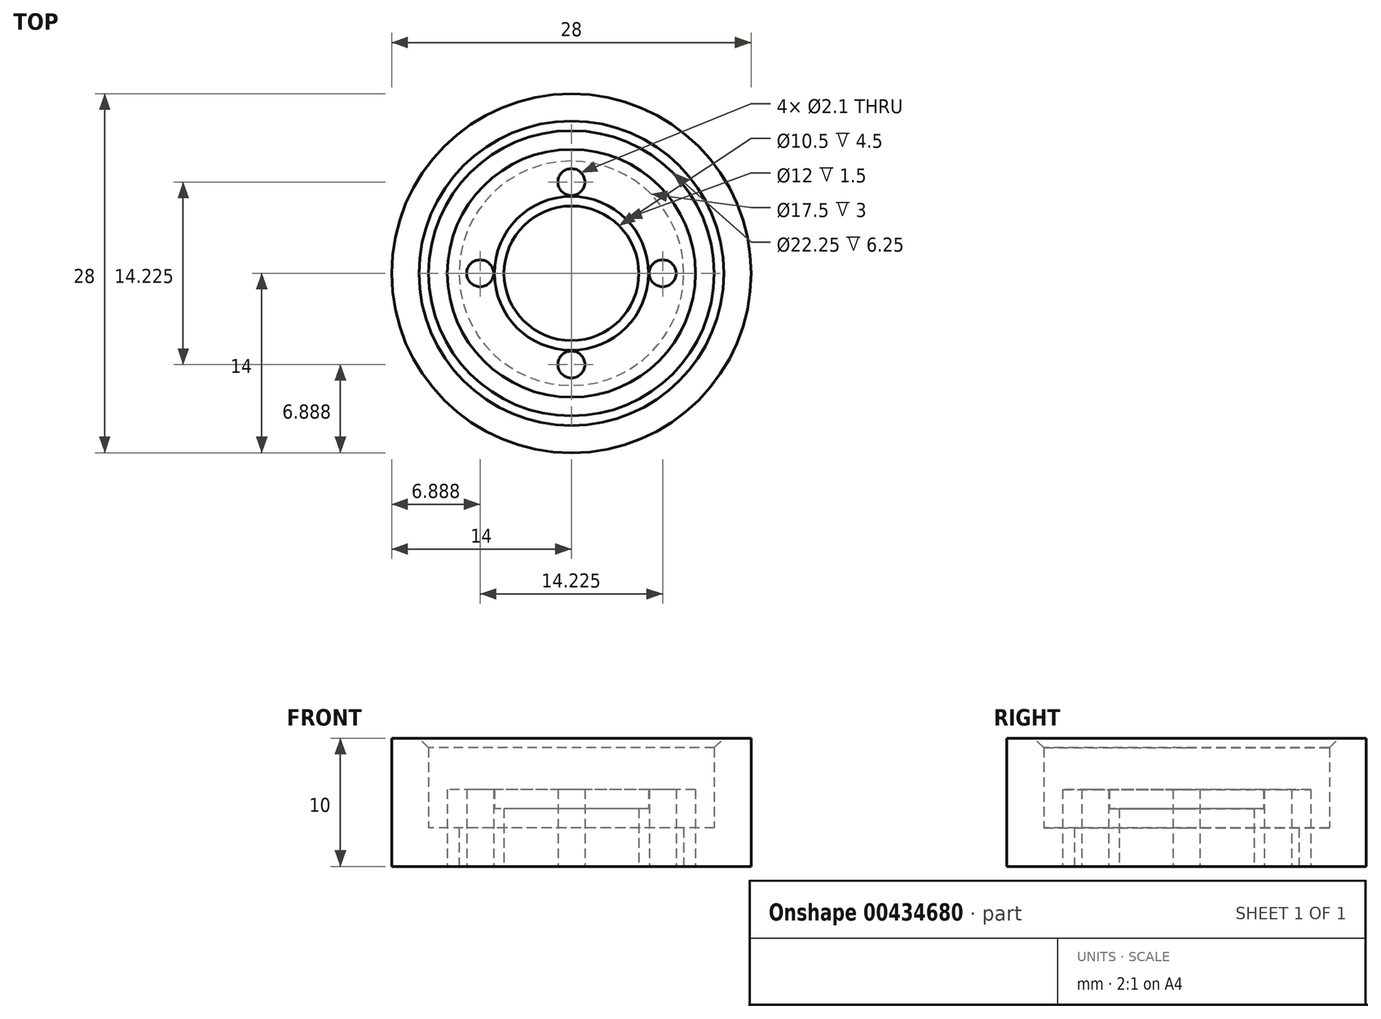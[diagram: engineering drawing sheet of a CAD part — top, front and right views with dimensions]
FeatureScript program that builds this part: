
annotation { "Feature Type Name" : "Feature", "Feature Type Description" : "" }
export const myFeature = defineFeature(function(context is Context, id is Id, definition is map)
    precondition{}
    {
        {
            assignVariable(context, id + "F0", {"name" : "BearingThickness", "anyValue" : 4});
        }
        {
            assignVariable(context, id + "F1", {"name" : "BearingDiameter", "anyValue" : 10.5});
        }
        {
            assignVariable(context, id + "F2", {"name" : "FlangeDiameter", "anyValue" : 12});
        }
        {
            assignVariable(context, id + "F3", {"name" : "FlangeThickness", "anyValue" : getVariable(context, 'FlangeDiameter') - getVariable(context, 'BearingDiameter')});
        }
        {
            assignVariable(context, id + "F4", {"name" : "HoleDiameter", "anyValue" : 2.1});
        }
        {
            assignVariable(context, id + "F5", {"name" : "HubThickness", "anyValue" : 0.5 + getVariable(context, 'BearingThickness') + getVariable(context, 'FlangeThickness')});
        }
        {
            var Q0;
            Q0=qCreatedBy(makeId("Top.planeOp"),FACE);
            var sketch = newSketch(context, id + "F6", { "sketchPlane" : qUnion([Q0])});
            skLineSegment(sketch, "E0", {"start": v(-35.9, 0) * mm, "end": v(35.9, 0) * mm, "construction": true});
            skLineSegment(sketch, "E1", {"start": v(0, 35.9) * mm, "end": v(0, -35.9) * mm, "construction": true});
            skCircle(sketch, "E2", {"center": v(0, 0) * mm, "radius": 5.25 * mm});
            skCircle(sketch, "E3", {"center": v(0, 0) * mm, "radius": 6 * mm});
            skCircle(sketch, "E4", {"center": v(0, 0) * mm, "radius": 6.06 * mm, "construction": true});
            skCircle(sketch, "E5.0", {"center": v(0, 0) * mm, "radius": 35.9 * mm});
            skCircle(sketch, "E6", {"center": v(-7.11, 0) * mm, "radius": 1.05 * mm, "construction": true});
            skCircle(sketch, "E7", {"center": v(0, 7.11) * mm, "radius": 1.05 * mm, "construction": true});
            skCircle(sketch, "E8.MirrorC", {"center": v(7.11, 0) * mm, "radius": 1.05 * mm, "construction": true});
            skCircle(sketch, "E9.MirrorC", {"center": v(0, -7.11) * mm, "radius": 1.05 * mm, "construction": true});
            skCircle(sketch, "E10", {"center": v(0, 0) * mm, "radius": 8.16 * mm, "construction": true});
            skCircle(sketch, "E11", {"center": v(0, 0) * mm, "radius": 9.66 * mm});
            skCircle(sketch, "E12.0", {"center": v(0, 0) * mm, "radius": 32.9 * mm});
            skLineSegment(sketch, "E12.1", {"start": v(-1.5, 39.75) * mm, "end": v(-1.5, 35.87) * mm});
            skLineSegment(sketch, "E12.2", {"start": v(1.5, 39.75) * mm, "end": v(1.5, 35.87) * mm});
            skArc(sketch, "E12.3", {"start": v(-0.3, 40.91) * mm, "mid": v(-1.15, 40.59) * mm, "end": v(-1.5, 39.75) * mm});
            skArc(sketch, "E12.4", {"start": v(0.3, 40.91) * mm, "mid": v(1.15, 40.59) * mm, "end": v(1.5, 39.75) * mm});
            skLineSegment(sketch, "E12.5", {"start": v(0.3, 40.91) * mm, "end": v(0, 40.92) * mm});
            skLineSegment(sketch, "E12.6", {"start": v(-0.3, 40.91) * mm, "end": v(0, 40.92) * mm});
            skLineSegment(sketch, "E13.1.1", {"start": v(-17.54, 35.7) * mm, "end": v(-15.96, 32.16) * mm});
            skLineSegment(sketch, "E13.1.2", {"start": v(-14.8, 36.92) * mm, "end": v(-13.22, 33.38) * mm});
            skArc(sketch, "E13.1.3", {"start": v(-16.92, 37.26) * mm, "mid": v(-17.56, 36.61) * mm, "end": v(-17.54, 35.7) * mm});
            skArc(sketch, "E13.1.4", {"start": v(-16.37, 37.5) * mm, "mid": v(-15.46, 37.54) * mm, "end": v(-14.8, 36.92) * mm});
            skLineSegment(sketch, "E13.1.5", {"start": v(-16.92, 37.26) * mm, "end": v(-16.64, 37.38) * mm});
            skLineSegment(sketch, "E13.1.6", {"start": v(-16.37, 37.5) * mm, "end": v(-16.64, 37.38) * mm});
            skLineSegment(sketch, "E13.2.1", {"start": v(-30.54, 25.48) * mm, "end": v(-27.66, 22.89) * mm});
            skLineSegment(sketch, "E13.2.2", {"start": v(-28.54, 27.71) * mm, "end": v(-25.65, 25.12) * mm});
            skArc(sketch, "E13.2.3", {"start": v(-30.6, 27.15) * mm, "mid": v(-30.93, 26.3) * mm, "end": v(-30.54, 25.48) * mm});
            skArc(sketch, "E13.2.4", {"start": v(-30.2, 27.6) * mm, "mid": v(-29.4, 28) * mm, "end": v(-28.54, 27.71) * mm});
            skLineSegment(sketch, "E13.2.5", {"start": v(-30.6, 27.15) * mm, "end": v(-30.4, 27.38) * mm});
            skLineSegment(sketch, "E13.2.6", {"start": v(-30.2, 27.6) * mm, "end": v(-30.4, 27.38) * mm});
            skLineSegment(sketch, "E13.3.1", {"start": v(-38.27, 10.86) * mm, "end": v(-34.58, 9.66) * mm});
            skLineSegment(sketch, "E13.3.2", {"start": v(-37.34, 13.71) * mm, "end": v(-33.65, 12.51) * mm});
            skArc(sketch, "E13.3.3", {"start": v(-39, 12.36) * mm, "mid": v(-38.95, 11.45) * mm, "end": v(-38.27, 10.86) * mm});
            skArc(sketch, "E13.3.4", {"start": v(-38.82, 12.93) * mm, "mid": v(-38.25, 13.63) * mm, "end": v(-37.34, 13.71) * mm});
            skLineSegment(sketch, "E13.3.5", {"start": v(-39, 12.36) * mm, "end": v(-38.91, 12.64) * mm});
            skLineSegment(sketch, "E13.3.6", {"start": v(-38.82, 12.93) * mm, "end": v(-38.91, 12.64) * mm});
            skLineSegment(sketch, "E13.4.1", {"start": v(-39.38, -5.65) * mm, "end": v(-35.52, -5.24) * mm});
            skLineSegment(sketch, "E13.4.2", {"start": v(-39.69, -2.66) * mm, "end": v(-35.83, -2.26) * mm});
            skArc(sketch, "E13.4.3", {"start": v(-40.66, -4.58) * mm, "mid": v(-40.24, -5.38) * mm, "end": v(-39.38, -5.65) * mm});
            skArc(sketch, "E13.4.4", {"start": v(-40.72, -3.98) * mm, "mid": v(-40.48, -3.1) * mm, "end": v(-39.69, -2.66) * mm});
            skLineSegment(sketch, "E13.4.5", {"start": v(-40.66, -4.58) * mm, "end": v(-40.7, -4.28) * mm});
            skLineSegment(sketch, "E13.4.6", {"start": v(-40.72, -3.98) * mm, "end": v(-40.7, -4.28) * mm});
            skLineSegment(sketch, "E13.5.1", {"start": v(-33.67, -21.17) * mm, "end": v(-30.31, -19.23) * mm});
            skLineSegment(sketch, "E13.5.2", {"start": v(-35.17, -18.58) * mm, "end": v(-31.81, -16.64) * mm});
            skArc(sketch, "E13.5.3", {"start": v(-35.28, -20.72) * mm, "mid": v(-34.58, -21.29) * mm, "end": v(-33.67, -21.17) * mm});
            skArc(sketch, "E13.5.4", {"start": v(-35.58, -20.2) * mm, "mid": v(-35.72, -19.3) * mm, "end": v(-35.17, -18.58) * mm});
            skLineSegment(sketch, "E13.5.5", {"start": v(-35.28, -20.72) * mm, "end": v(-35.44, -20.46) * mm});
            skLineSegment(sketch, "E13.5.6", {"start": v(-35.58, -20.2) * mm, "end": v(-35.44, -20.46) * mm});
            skLineSegment(sketch, "E13.6.1", {"start": v(-22.15, -33.04) * mm, "end": v(-19.87, -29.9) * mm});
            skLineSegment(sketch, "E13.6.2", {"start": v(-24.58, -31.28) * mm, "end": v(-22.3, -28.14) * mm});
            skArc(sketch, "E13.6.3", {"start": v(-23.8, -33.28) * mm, "mid": v(-22.93, -33.5) * mm, "end": v(-22.15, -33.04) * mm});
            skArc(sketch, "E13.6.4", {"start": v(-24.3, -32.92) * mm, "mid": v(-24.78, -32.16) * mm, "end": v(-24.58, -31.28) * mm});
            skLineSegment(sketch, "E13.6.5", {"start": v(-23.8, -33.28) * mm, "end": v(-24.05, -33.1) * mm});
            skLineSegment(sketch, "E13.6.6", {"start": v(-24.3, -32.92) * mm, "end": v(-24.05, -33.1) * mm});
            skLineSegment(sketch, "E13.7.1", {"start": v(-6.8, -39.2) * mm, "end": v(-6, -35.4) * mm});
            skLineSegment(sketch, "E13.7.2", {"start": v(-9.73, -38.57) * mm, "end": v(-8.92, -34.77) * mm});
            skArc(sketch, "E13.7.3", {"start": v(-8.21, -40.08) * mm, "mid": v(-7.32, -39.94) * mm, "end": v(-6.8, -39.2) * mm});
            skArc(sketch, "E13.7.4", {"start": v(-8.8, -39.96) * mm, "mid": v(-9.56, -39.46) * mm, "end": v(-9.73, -38.57) * mm});
            skLineSegment(sketch, "E13.7.5", {"start": v(-8.21, -40.08) * mm, "end": v(-8.5, -40.02) * mm});
            skLineSegment(sketch, "E13.7.6", {"start": v(-8.8, -39.96) * mm, "end": v(-8.5, -40.02) * mm});
            skLineSegment(sketch, "E13.8.1", {"start": v(9.73, -38.57) * mm, "end": v(8.92, -34.77) * mm});
            skLineSegment(sketch, "E13.8.2", {"start": v(6.8, -39.2) * mm, "end": v(6, -35.4) * mm});
            skArc(sketch, "E13.8.3", {"start": v(8.8, -39.96) * mm, "mid": v(9.56, -39.46) * mm, "end": v(9.73, -38.57) * mm});
            skArc(sketch, "E13.8.4", {"start": v(8.21, -40.08) * mm, "mid": v(7.32, -39.94) * mm, "end": v(6.8, -39.2) * mm});
            skLineSegment(sketch, "E13.8.5", {"start": v(8.8, -39.96) * mm, "end": v(8.5, -40.02) * mm});
            skLineSegment(sketch, "E13.8.6", {"start": v(8.21, -40.08) * mm, "end": v(8.5, -40.02) * mm});
            skLineSegment(sketch, "E13.9.1", {"start": v(24.58, -31.28) * mm, "end": v(22.3, -28.14) * mm});
            skLineSegment(sketch, "E13.9.2", {"start": v(22.15, -33.04) * mm, "end": v(19.87, -29.9) * mm});
            skArc(sketch, "E13.9.3", {"start": v(24.3, -32.92) * mm, "mid": v(24.78, -32.16) * mm, "end": v(24.58, -31.28) * mm});
            skArc(sketch, "E13.9.4", {"start": v(23.8, -33.28) * mm, "mid": v(22.93, -33.5) * mm, "end": v(22.15, -33.04) * mm});
            skLineSegment(sketch, "E13.9.5", {"start": v(24.3, -32.92) * mm, "end": v(24.05, -33.1) * mm});
            skLineSegment(sketch, "E13.9.6", {"start": v(23.8, -33.28) * mm, "end": v(24.05, -33.1) * mm});
            skLineSegment(sketch, "E13.10.1", {"start": v(35.17, -18.58) * mm, "end": v(31.81, -16.64) * mm});
            skLineSegment(sketch, "E13.10.2", {"start": v(33.67, -21.17) * mm, "end": v(30.31, -19.23) * mm});
            skArc(sketch, "E13.10.3", {"start": v(35.58, -20.2) * mm, "mid": v(35.72, -19.3) * mm, "end": v(35.17, -18.58) * mm});
            skArc(sketch, "E13.10.4", {"start": v(35.28, -20.72) * mm, "mid": v(34.58, -21.29) * mm, "end": v(33.67, -21.17) * mm});
            skLineSegment(sketch, "E13.10.5", {"start": v(35.58, -20.2) * mm, "end": v(35.44, -20.46) * mm});
            skLineSegment(sketch, "E13.10.6", {"start": v(35.28, -20.72) * mm, "end": v(35.44, -20.46) * mm});
            skLineSegment(sketch, "E13.11.1", {"start": v(39.69, -2.66) * mm, "end": v(35.83, -2.26) * mm});
            skLineSegment(sketch, "E13.11.2", {"start": v(39.38, -5.65) * mm, "end": v(35.52, -5.24) * mm});
            skArc(sketch, "E13.11.3", {"start": v(40.72, -3.98) * mm, "mid": v(40.48, -3.1) * mm, "end": v(39.69, -2.66) * mm});
            skArc(sketch, "E13.11.4", {"start": v(40.66, -4.58) * mm, "mid": v(40.24, -5.38) * mm, "end": v(39.38, -5.65) * mm});
            skLineSegment(sketch, "E13.11.5", {"start": v(40.72, -3.98) * mm, "end": v(40.7, -4.28) * mm});
            skLineSegment(sketch, "E13.11.6", {"start": v(40.66, -4.58) * mm, "end": v(40.7, -4.28) * mm});
            skLineSegment(sketch, "E13.12.1", {"start": v(37.34, 13.71) * mm, "end": v(33.65, 12.51) * mm});
            skLineSegment(sketch, "E13.12.2", {"start": v(38.27, 10.86) * mm, "end": v(34.58, 9.66) * mm});
            skArc(sketch, "E13.12.3", {"start": v(38.82, 12.93) * mm, "mid": v(38.25, 13.63) * mm, "end": v(37.34, 13.71) * mm});
            skArc(sketch, "E13.12.4", {"start": v(39, 12.36) * mm, "mid": v(38.95, 11.45) * mm, "end": v(38.27, 10.86) * mm});
            skLineSegment(sketch, "E13.12.5", {"start": v(38.82, 12.93) * mm, "end": v(38.91, 12.64) * mm});
            skLineSegment(sketch, "E13.12.6", {"start": v(39, 12.36) * mm, "end": v(38.91, 12.64) * mm});
            skLineSegment(sketch, "E13.13.1", {"start": v(28.54, 27.71) * mm, "end": v(25.65, 25.12) * mm});
            skLineSegment(sketch, "E13.13.2", {"start": v(30.54, 25.48) * mm, "end": v(27.66, 22.89) * mm});
            skArc(sketch, "E13.13.3", {"start": v(30.2, 27.6) * mm, "mid": v(29.4, 28) * mm, "end": v(28.54, 27.71) * mm});
            skArc(sketch, "E13.13.4", {"start": v(30.6, 27.15) * mm, "mid": v(30.93, 26.3) * mm, "end": v(30.54, 25.48) * mm});
            skLineSegment(sketch, "E13.13.5", {"start": v(30.2, 27.6) * mm, "end": v(30.4, 27.38) * mm});
            skLineSegment(sketch, "E13.13.6", {"start": v(30.6, 27.15) * mm, "end": v(30.4, 27.38) * mm});
            skLineSegment(sketch, "E13.14.1", {"start": v(14.8, 36.92) * mm, "end": v(13.22, 33.38) * mm});
            skLineSegment(sketch, "E13.14.2", {"start": v(17.54, 35.7) * mm, "end": v(15.96, 32.16) * mm});
            skArc(sketch, "E13.14.3", {"start": v(16.37, 37.5) * mm, "mid": v(15.46, 37.54) * mm, "end": v(14.8, 36.92) * mm});
            skArc(sketch, "E13.14.4", {"start": v(16.92, 37.26) * mm, "mid": v(17.56, 36.61) * mm, "end": v(17.54, 35.7) * mm});
            skLineSegment(sketch, "E13.14.5", {"start": v(16.37, 37.5) * mm, "end": v(16.64, 37.38) * mm});
            skLineSegment(sketch, "E13.14.6", {"start": v(16.92, 37.26) * mm, "end": v(16.64, 37.38) * mm});
            skSolve(sketch);
        }
        {
            var Q0;
            Q0=makeQuery(id+"F6.imprint","IMPRINT",FACE,{"disambiguationData":[TD([[makeQuery(id+"F6.imprint","IMPRINT",EDGE,{"derivedFrom":sQuery(id+"F6.wireOp",EDGE,"E2")}),-1.0]])]});
            extrude(context, id + "F7", {"entities" : qUnion([Q0]), "depth" : (getVariable(context, 'HubThickness') - getVariable(context, 'FlangeThickness')) * mm});
        }
        {
            var Q0;
            Q0=makeQuery(id+"F6.imprint","IMPRINT",FACE,{"disambiguationData":[TD([[makeQuery(id+"F6.imprint","IMPRINT",EDGE,{"derivedFrom":sQuery(id+"F6.wireOp",EDGE,"E3")}),-1.0]])]});
            var Q1;
            Q1=sQuery(id+"F6.wireOp",EDGE,"E11");
            var Q2;
            Q2=sQuery(id+"F6.wireOp",EDGE,"E3");
            extrude(context, id + "F8", {"entities" : qUnion([Q0]), "operationType" : NewBodyOperationType.ADD, "surfaceEntities" : qUnion([Q1, Q2]), "depth" : (getVariable(context, 'HubThickness')) * mm});
        }
        {
            var Q0;
            Q0=sQuery(id+"F6.wireOp",VERTEX,"E7.center");
            var Q1;
            Q1=sQuery(id+"F6.wireOp",VERTEX,"E8.MirrorC.center");
            var Q2;
            Q2=sQuery(id+"F6.wireOp",VERTEX,"E6.center");
            var Q3;
            Q3=sQuery(id+"F6.wireOp",VERTEX,"E9.MirrorC.center");
            var Q4;
            Q4=makeQuery(id+"F7.opExtrude","SWEPT_BODY",BODY,{"disambiguationData":[OSD([sQuery(id+"F6.wireOp",EDGE,"E2"),sQuery(id+"F6.wireOp",EDGE,"E3")])]});
            hole(context, id + "F9", {"style" : HoleStyle.SIMPLE, "endStyle" : HoleEndStyle.THROUGH, "oppositeDirection" : true, "holeDiameter" : getVariable(context, 'HoleDiameter') * mm, "isTappedThrough" : true, "tappedDepth" : 12 * mm, "tapClearance" : 3, "locations" : qUnion([Q0, Q1, Q2, Q3]), "scope" : qUnion([Q4])});
        }
        {
            var Q0;
            Q0=qCreatedBy(makeId("Top.planeOp"),FACE);
            var sketch = newSketch(context, id + "F10", { "sketchPlane" : qUnion([Q0])});
            skLineSegment(sketch, "E14.0", {"start": v(-35.9, 0) * mm, "end": v(35.9, 0) * mm, "construction": true});
            skLineSegment(sketch, "E14.1", {"start": v(0, 35.9) * mm, "end": v(0, -35.9) * mm, "construction": true});
            skCircle(sketch, "E15.0", {"center": v(0, 0) * mm, "radius": 32.9 * mm, "construction": true});
            skCircle(sketch, "E16", {"center": v(0, 0) * mm, "radius": 8.75 * mm});
            skCircle(sketch, "E17", {"center": v(0, 0) * mm, "radius": 11.12 * mm});
            skCircle(sketch, "E18", {"center": v(0, 0) * mm, "radius": 14 * mm});
            skSolve(sketch);
        }
        {
            var Q0;
            Q0=makeQuery(id+"F10.imprint","IMPRINT",FACE,{"disambiguationData":[TD([[makeQuery(id+"F10.imprint","IMPRINT",EDGE,{"derivedFrom":sQuery(id+"F10.wireOp",EDGE,"E17")}),-1.0]])]});
            var Q1;
            Q1=makeQuery(id+"F10.imprint","IMPRINT",FACE,{"disambiguationData":[TD([[makeQuery(id+"F10.imprint","IMPRINT",EDGE,{"derivedFrom":sQuery(id+"F10.wireOp",EDGE,"E16")}),-1.0]])]});
            extrude(context, id + "F11", {"entities" : qUnion([Q0, Q1]), "depth" : 3 * mm});
        }
        {
            var Q0;
            Q0=makeQuery(id+"F10.imprint","IMPRINT",FACE,{"disambiguationData":[TD([[makeQuery(id+"F10.imprint","IMPRINT",EDGE,{"derivedFrom":sQuery(id+"F10.wireOp",EDGE,"E17")}),-1.0]])]});
            var sketch = newSketch(context, id + "F12", { "sketchPlane" : qUnion([Q0])});
            skCircle(sketch, "E19.0", {"center": v(0, 0) * mm, "radius": 11.12 * mm});
            skCircle(sketch, "E19.1", {"center": v(0, 0) * mm, "radius": 14 * mm});
            skSolve(sketch);
        }
        {
            var Q0;
            Q0=makeQuery(id+"F12.imprint","IMPRINT",FACE,{"disambiguationData":[TD([[makeQuery(id+"F12.imprint","IMPRINT",EDGE,{"derivedFrom":sQuery(id+"F12.wireOp",EDGE,"E19.0")}),-1.0]])]});
            extrude(context, id + "F13", {"entities" : qUnion([Q0]), "operationType" : NewBodyOperationType.ADD, "depth" : 10 * mm});
        }
        {
            var Q0;
            Q0=makeQuery(id+"F13.opExtrude","CAP_EDGE",EDGE,{"disambiguationData":[OSD([sQuery(id+"F12.wireOp",EDGE,"E19.0")])],"isStart":false});
            chamfer(context, id + "F14", {"entities" : qUnion([Q0]), "width" : 0.75 * mm, "tangentPropagation" : true});
        }
    });
